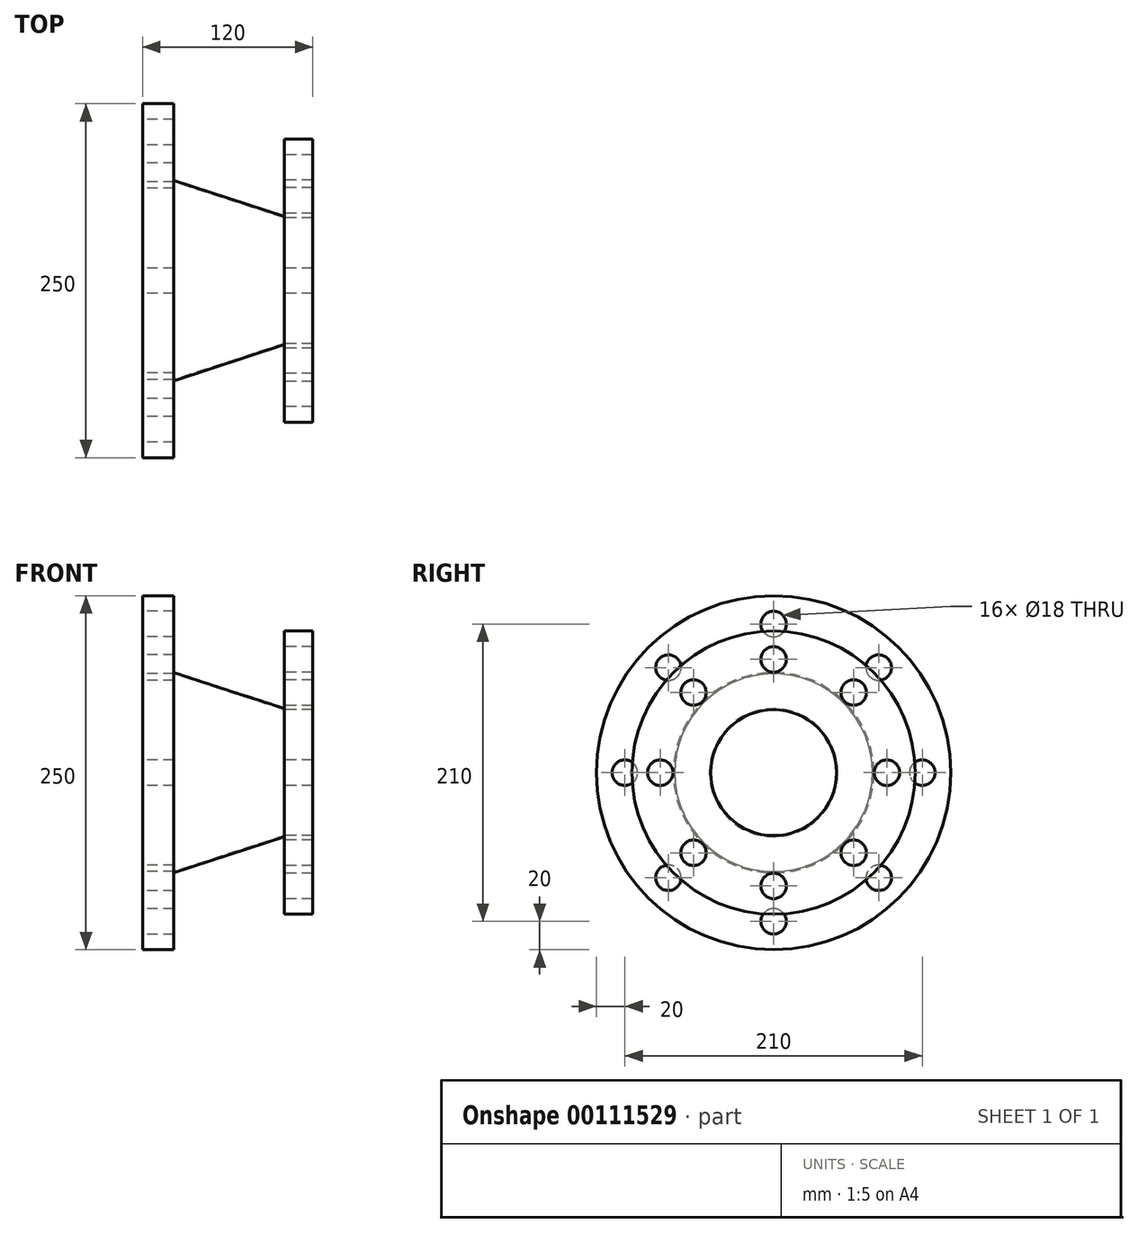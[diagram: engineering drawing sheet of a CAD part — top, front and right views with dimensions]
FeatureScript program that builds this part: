
annotation { "Feature Type Name" : "Feature", "Feature Type Description" : "" }
export const myFeature = defineFeature(function(context is Context, id is Id, definition is map)
    precondition{}
    {
        {
            var Q0;
            Q0=qCreatedBy(makeId("Right.planeOp"),FACE);
            var sketch = newSketch(context, id + "F0", { "sketchPlane" : qUnion([Q0])});
            skCircle(sketch, "E0", {"center": v(0, 0) * mm, "radius": 70.75 * mm});
            skCircle(sketch, "E1", {"center": v(0, 0) * mm, "radius": 105 * mm, "construction": true});
            skCircle(sketch, "E2", {"center": v(0, 0) * mm, "radius": 125 * mm});
            skCircle(sketch, "E3", {"center": v(0, -105) * mm, "radius": 9 * mm});
            skCircle(sketch, "E4.1.0", {"center": v(74.25, -74.25) * mm, "radius": 9 * mm});
            skCircle(sketch, "E4.2.0", {"center": v(105, 0) * mm, "radius": 9 * mm});
            skCircle(sketch, "E4.3.0", {"center": v(74.25, 74.25) * mm, "radius": 9 * mm});
            skCircle(sketch, "E4.4.0", {"center": v(0, 105) * mm, "radius": 9 * mm});
            skCircle(sketch, "E4.5.0", {"center": v(-74.25, 74.25) * mm, "radius": 9 * mm});
            skCircle(sketch, "E4.6.0", {"center": v(-105, 0) * mm, "radius": 9 * mm});
            skCircle(sketch, "E4.7.0", {"center": v(-74.25, -74.25) * mm, "radius": 9 * mm});
            skCircle(sketch, "E5", {"center": v(0, 0) * mm, "radius": 69.85 * mm});
            skSolve(sketch);
        }
        {
            var Q0;
            Q0=qSketchRegion(id+"F0",true);
            var Q1;
            Q1=makeQuery(id+"F0.imprint","IMPRINT",FACE,{"disambiguationData":[TD([[makeQuery(id+"F0.imprint","IMPRINT",EDGE,{"derivedFrom":sQuery(id+"F0.wireOp",EDGE,"E0")}),1.0]])]});
            extrude(context, id + "F1", {"entities" : qUnion([Q0, Q1]), "depth" : 22 * mm});
        }
        {
            var Q0;
            Q0=qCreatedBy(makeId("Right.planeOp"),FACE);
            cPlane(context, id + "F2", {"entities" : qUnion([Q0]), "cplaneType" : CPlaneType.OFFSET, "offset" : 100 * mm, "width" : 150 * mm, "height" : 150 * mm});
        }
        {
            var Q0;
            Q0=qCreatedBy(id+"F2.planeOp",FACE);
            var sketch = newSketch(context, id + "F3", { "sketchPlane" : qUnion([Q0])});
            skCircle(sketch, "E6", {"center": v(0, 0) * mm, "radius": 45.25 * mm});
            skCircle(sketch, "E7", {"center": v(0, 0) * mm, "radius": 80 * mm, "construction": true});
            skCircle(sketch, "E8", {"center": v(0, 0) * mm, "radius": 100 * mm});
            skCircle(sketch, "E9", {"center": v(0, -80) * mm, "radius": 9 * mm});
            skCircle(sketch, "E10.1.0", {"center": v(56.57, -56.57) * mm, "radius": 9 * mm});
            skCircle(sketch, "E10.2.0", {"center": v(80, 0) * mm, "radius": 9 * mm});
            skCircle(sketch, "E10.3.0", {"center": v(56.57, 56.57) * mm, "radius": 9 * mm});
            skCircle(sketch, "E10.4.0", {"center": v(0, 80) * mm, "radius": 9 * mm});
            skCircle(sketch, "E10.5.0", {"center": v(-56.57, 56.57) * mm, "radius": 9 * mm});
            skCircle(sketch, "E10.6.0", {"center": v(-80, 0) * mm, "radius": 9 * mm});
            skCircle(sketch, "E10.7.0", {"center": v(-56.57, -56.57) * mm, "radius": 9 * mm});
            skCircle(sketch, "E11", {"center": v(0, 0) * mm, "radius": 44.45 * mm});
            skSolve(sketch);
        }
        {
            var Q0;
            Q0=qSketchRegion(id+"F3",true);
            var Q1;
            Q1=makeQuery(id+"F3.imprint","IMPRINT",FACE,{"disambiguationData":[TD([[makeQuery(id+"F3.imprint","IMPRINT",EDGE,{"derivedFrom":sQuery(id+"F3.wireOp",EDGE,"E6")}),1.0]])]});
            extrude(context, id + "F4", {"entities" : qUnion([Q0, Q1]), "depth" : 20 * mm});
        }
        {
            var Q0;
            Q0=makeQuery(id+"F1.opExtrude","CAP_FACE",FACE,{"disambiguationData":[OSD([sQuery(id+"F0.wireOp",EDGE,"E2"),sQuery(id+"F0.wireOp",EDGE,"E3"),sQuery(id+"F0.wireOp",EDGE,"E4.1.0"),sQuery(id+"F0.wireOp",EDGE,"E4.2.0"),sQuery(id+"F0.wireOp",EDGE,"E4.3.0"),sQuery(id+"F0.wireOp",EDGE,"E4.4.0"),sQuery(id+"F0.wireOp",EDGE,"E4.5.0"),sQuery(id+"F0.wireOp",EDGE,"E4.6.0"),sQuery(id+"F0.wireOp",EDGE,"E4.7.0"),sQuery(id+"F0.wireOp",EDGE,"E5")])],"isStart":false});
            var sketch = newSketch(context, id + "F5", { "sketchPlane" : qUnion([Q0])});
            skCircle(sketch, "E12.0", {"center": v(0, 0) * mm, "radius": 69.85 * mm});
            skCircle(sketch, "E12.1", {"center": v(0, 0) * mm, "radius": 70.75 * mm});
            skSolve(sketch);
        }
        {
            var Q0;
            Q0=qCreatedBy(makeId("Front.planeOp"),FACE);
            var sketch = newSketch(context, id + "F6", { "sketchPlane" : qUnion([Q0])});
            skLineSegment(sketch, "E13", {"start": v(-37.48, 0) * mm, "end": v(202.14, 0) * mm, "construction": true});
            skLineSegment(sketch, "E14.0", {"start": v(22, 70.75) * mm, "end": v(22, -70.75) * mm});
            skLineSegment(sketch, "E15.0", {"start": v(22, 69.85) * mm, "end": v(22, -69.85) * mm});
            skLineSegment(sketch, "E16.0", {"start": v(100, 45.25) * mm, "end": v(100, -45.25) * mm});
            skLineSegment(sketch, "E17.0", {"start": v(100, 44.45) * mm, "end": v(100, -44.45) * mm});
            skLineSegment(sketch, "E18", {"start": v(100, 45.25) * mm, "end": v(22, 70.75) * mm});
            skLineSegment(sketch, "E19", {"start": v(22, 69.85) * mm, "end": v(100, 44.45) * mm});
            skSolve(sketch);
        }
        {
            var Q0;
            Q0=qSketchRegion(id+"F6",true);
            var Q1;
            Q1=sQuery(id+"F6.wireOp",EDGE,"E13");
            revolve(context, id + "F7", {"operationType" : NewBodyOperationType.ADD, "entities" : qUnion([Q0]), "axis" : qUnion([Q1]), "revolveType" : RevolveType.FULL});
        }
    });
